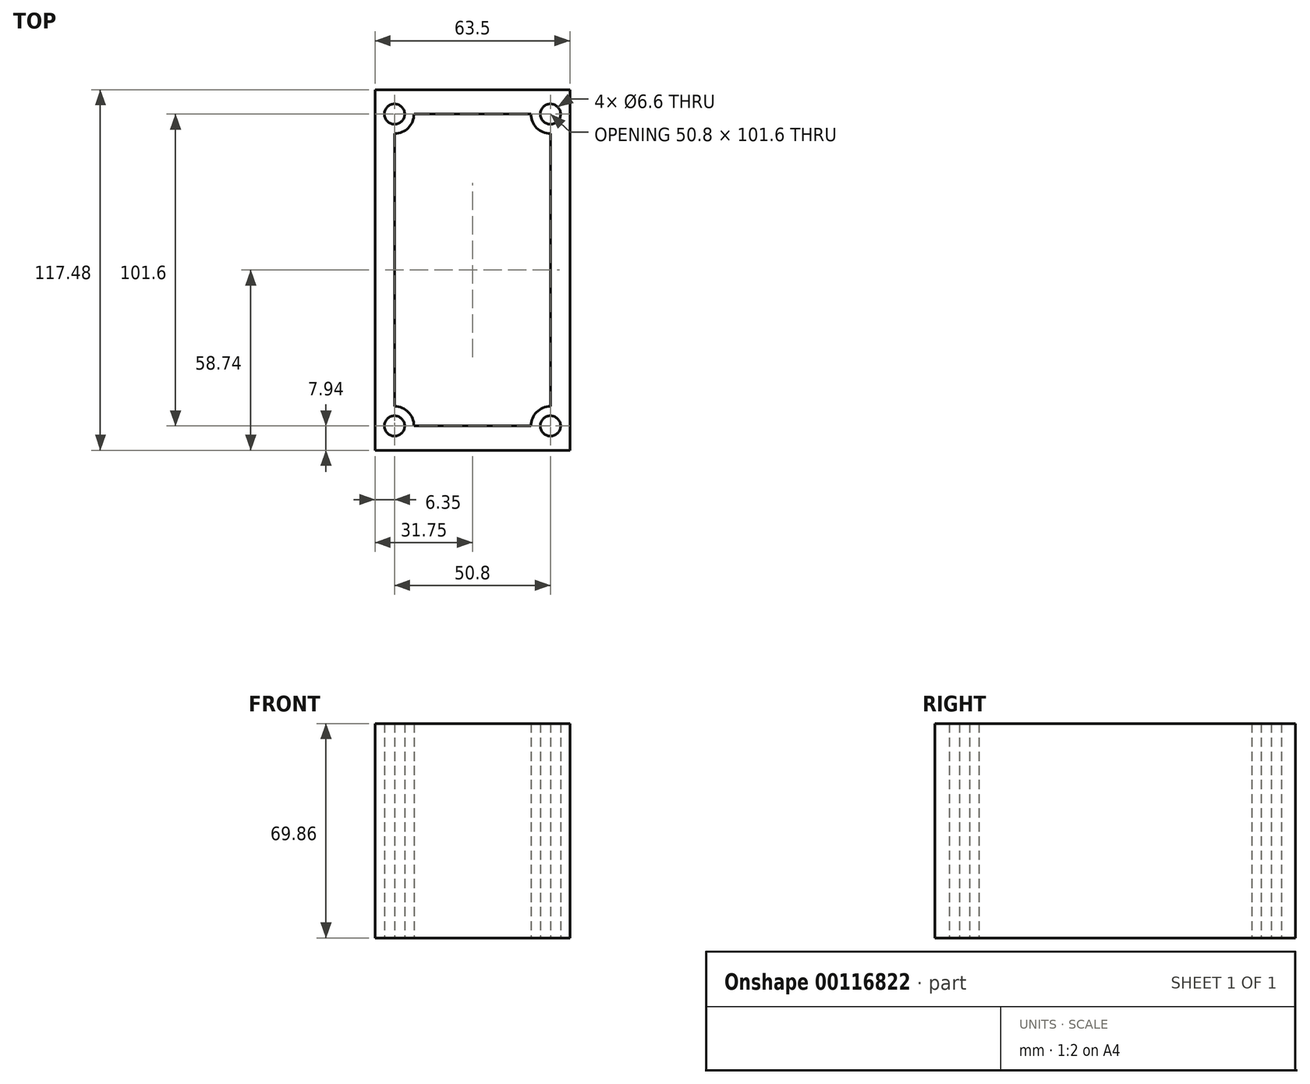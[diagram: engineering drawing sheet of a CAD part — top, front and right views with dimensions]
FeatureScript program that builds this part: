
annotation { "Feature Type Name" : "Feature", "Feature Type Description" : "" }
export const myFeature = defineFeature(function(context is Context, id is Id, definition is map)
    precondition{}
    {
        {
            var Q0;
            Q0=qCreatedBy(makeId("Top.planeOp"),FACE);
            var sketch = newSketch(context, id + "F0", { "sketchPlane" : qUnion([Q0])});
            skLineSegment(sketch, "E0.bottom", {"start": v(31.75, -58.74) * mm, "end": v(-31.75, -58.74) * mm});
            skLineSegment(sketch, "E0.top", {"start": v(31.75, 58.74) * mm, "end": v(-31.75, 58.74) * mm});
            skLineSegment(sketch, "E0.left", {"start": v(31.75, -58.74) * mm, "end": v(31.75, 58.74) * mm});
            skLineSegment(sketch, "E0.right", {"start": v(-31.75, -58.74) * mm, "end": v(-31.75, 58.74) * mm});
            skPoint(sketch, "E0.middle", {"position": v(0, 0) * mm});
            skLineSegment(sketch, "E1.bottom", {"start": v(25.4, 50.8) * mm, "end": v(-25.4, 50.8) * mm});
            skLineSegment(sketch, "E1.top", {"start": v(25.4, -50.8) * mm, "end": v(-25.4, -50.8) * mm});
            skLineSegment(sketch, "E1.left", {"start": v(25.4, 50.8) * mm, "end": v(25.4, -50.8) * mm});
            skLineSegment(sketch, "E1.right", {"start": v(-25.4, 50.8) * mm, "end": v(-25.4, -50.8) * mm});
            skCircle(sketch, "E2", {"center": v(-25.4, 50.8) * mm, "radius": 3.3 * mm});
            skCircle(sketch, "E3", {"center": v(25.4, 50.8) * mm, "radius": 3.3 * mm});
            skCircle(sketch, "E4", {"center": v(-25.4, -50.8) * mm, "radius": 3.3 * mm});
            skCircle(sketch, "E5", {"center": v(25.4, -50.8) * mm, "radius": 3.3 * mm});
            skCircle(sketch, "E6", {"center": v(-25.4, 50.8) * mm, "radius": 6.35 * mm});
            skCircle(sketch, "E7", {"center": v(25.4, 50.8) * mm, "radius": 6.35 * mm});
            skCircle(sketch, "E8", {"center": v(25.4, -50.8) * mm, "radius": 6.35 * mm});
            skCircle(sketch, "E9", {"center": v(-25.4, -50.8) * mm, "radius": 6.35 * mm});
            skSolve(sketch);
        }
        {
            var Q0;
            {var subQ0=sQuery(id+"F0.wireOp",EDGE,"E9");var subQ1=sQuery(id+"F0.wireOp",EDGE,"E0.right");var subQ2=makeQuery(id+"F0.imprint","INTERSECT",VERTEX,{"derivedFrom":[subQ1,subQ0]});Q0=makeQuery(id+"F0.imprint","IMPRINT",FACE,{"disambiguationData":[TD([[makeQuery(id+"F0.imprint","IMPRINT",EDGE,{"disambiguationData":[TD([[subQ2,-1.0]])],"derivedFrom":subQ1}),-1.0]])]});}
            var Q1;
            {var subQ6=sQuery(id+"F0.wireOp",EDGE,"E0.top");Q1=makeQuery(id+"F0.imprint","IMPRINT",FACE,{"disambiguationData":[TD([[makeQuery(id+"F0.imprint","IMPRINT",EDGE,{"derivedFrom":subQ6}),1.0]])]});}
            var Q2;
            {var subQ1=sQuery(id+"F0.wireOp",EDGE,"E1.bottom");var subQ5=sQuery(id+"F0.wireOp",EDGE,"E6");var subQ8=makeQuery(id+"F0.imprint","INTERSECT",VERTEX,{"derivedFrom":[subQ1,subQ5]});Q2=makeQuery(id+"F0.imprint","IMPRINT",FACE,{"disambiguationData":[TD([[makeQuery(id+"F0.imprint","IMPRINT",EDGE,{"disambiguationData":[TD([[subQ8,-1.0]])],"derivedFrom":subQ1}),-1.0]])]});}
            var Q3;
            {var subQ0=sQuery(id+"F0.wireOp",EDGE,"E6");var subQ1=sQuery(id+"F0.wireOp",EDGE,"E1.bottom");var subQ2=makeQuery(id+"F0.imprint","INTERSECT",VERTEX,{"derivedFrom":[subQ1,subQ0]});Q3=makeQuery(id+"F0.imprint","IMPRINT",FACE,{"disambiguationData":[TD([[makeQuery(id+"F0.imprint","IMPRINT",EDGE,{"disambiguationData":[TD([[subQ2,-1.0]])],"derivedFrom":subQ1}),1.0]])]});}
            var Q4;
            {var subQ0=sQuery(id+"F0.wireOp",EDGE,"E9");var subQ1=sQuery(id+"F0.wireOp",EDGE,"E1.top");var subQ2=makeQuery(id+"F0.imprint","INTERSECT",VERTEX,{"derivedFrom":[subQ1,subQ0]});Q4=makeQuery(id+"F0.imprint","IMPRINT",FACE,{"disambiguationData":[TD([[makeQuery(id+"F0.imprint","IMPRINT",EDGE,{"disambiguationData":[TD([[subQ2,-1.0]])],"derivedFrom":subQ1}),-1.0]])]});}
            var Q5;
            {var subQ1=sQuery(id+"F0.wireOp",EDGE,"E1.top");var subQ5=sQuery(id+"F0.wireOp",EDGE,"E9");var subQ8=makeQuery(id+"F0.imprint","INTERSECT",VERTEX,{"derivedFrom":[subQ1,subQ5]});Q5=makeQuery(id+"F0.imprint","IMPRINT",FACE,{"disambiguationData":[TD([[makeQuery(id+"F0.imprint","IMPRINT",EDGE,{"disambiguationData":[TD([[subQ8,-1.0]])],"derivedFrom":subQ1}),1.0]])]});}
            var Q6;
            {var subQ1=sQuery(id+"F0.wireOp",EDGE,"E0.bottom");Q6=makeQuery(id+"F0.imprint","IMPRINT",FACE,{"disambiguationData":[TD([[makeQuery(id+"F0.imprint","IMPRINT",EDGE,{"derivedFrom":subQ1}),-1.0]])]});}
            var Q7;
            {var subQ4=sQuery(id+"F0.wireOp",EDGE,"E5");var subQ5=sQuery(id+"F0.wireOp",EDGE,"E1.top");var subQ6=makeQuery(id+"F0.imprint","INTERSECT",VERTEX,{"derivedFrom":[subQ5,subQ4]});Q7=makeQuery(id+"F0.imprint","IMPRINT",FACE,{"disambiguationData":[TD([[makeQuery(id+"F0.imprint","IMPRINT",EDGE,{"disambiguationData":[TD([[subQ6,-1.0]])],"derivedFrom":subQ5}),1.0]])]});}
            var Q8;
            {var subQ0=sQuery(id+"F0.wireOp",EDGE,"E5");var subQ1=sQuery(id+"F0.wireOp",EDGE,"E1.top");var subQ2=makeQuery(id+"F0.imprint","INTERSECT",VERTEX,{"derivedFrom":[subQ1,subQ0]});Q8=makeQuery(id+"F0.imprint","IMPRINT",FACE,{"disambiguationData":[TD([[makeQuery(id+"F0.imprint","IMPRINT",EDGE,{"disambiguationData":[TD([[subQ2,-1.0]])],"derivedFrom":subQ1}),-1.0]])]});}
            var Q9;
            {var subQ0=sQuery(id+"F0.wireOp",EDGE,"E3");var subQ1=sQuery(id+"F0.wireOp",EDGE,"E1.bottom");var subQ2=makeQuery(id+"F0.imprint","INTERSECT",VERTEX,{"derivedFrom":[subQ1,subQ0]});Q9=makeQuery(id+"F0.imprint","IMPRINT",FACE,{"disambiguationData":[TD([[makeQuery(id+"F0.imprint","IMPRINT",EDGE,{"disambiguationData":[TD([[subQ2,-1.0]])],"derivedFrom":subQ1}),-1.0]])]});}
            var Q10;
            {var subQ0=sQuery(id+"F0.wireOp",EDGE,"E3");var subQ1=sQuery(id+"F0.wireOp",EDGE,"E1.bottom");var subQ2=makeQuery(id+"F0.imprint","INTERSECT",VERTEX,{"derivedFrom":[subQ1,subQ0]});Q10=makeQuery(id+"F0.imprint","IMPRINT",FACE,{"disambiguationData":[TD([[makeQuery(id+"F0.imprint","IMPRINT",EDGE,{"disambiguationData":[TD([[subQ2,-1.0]])],"derivedFrom":subQ1}),1.0]])]});}
            var Q11;
            {var subQ0=sQuery(id+"F0.wireOp",EDGE,"E8");var subQ1=sQuery(id+"F0.wireOp",EDGE,"E0.left");var subQ2=makeQuery(id+"F0.imprint","INTERSECT",VERTEX,{"derivedFrom":[subQ1,subQ0]});Q11=makeQuery(id+"F0.imprint","IMPRINT",FACE,{"disambiguationData":[TD([[makeQuery(id+"F0.imprint","IMPRINT",EDGE,{"disambiguationData":[TD([[subQ2,-1.0]])],"derivedFrom":subQ1}),1.0]])]});}
            extrude(context, id + "F1", {"entities" : qUnion([Q0, Q1, Q2, Q3, Q4, Q5, Q6, Q7, Q8, Q9, Q10, Q11]), "depth" : 69.85 * mm, "offsetDistance" : 25.4 * mm, "symmetric" : true});
        }
    });
